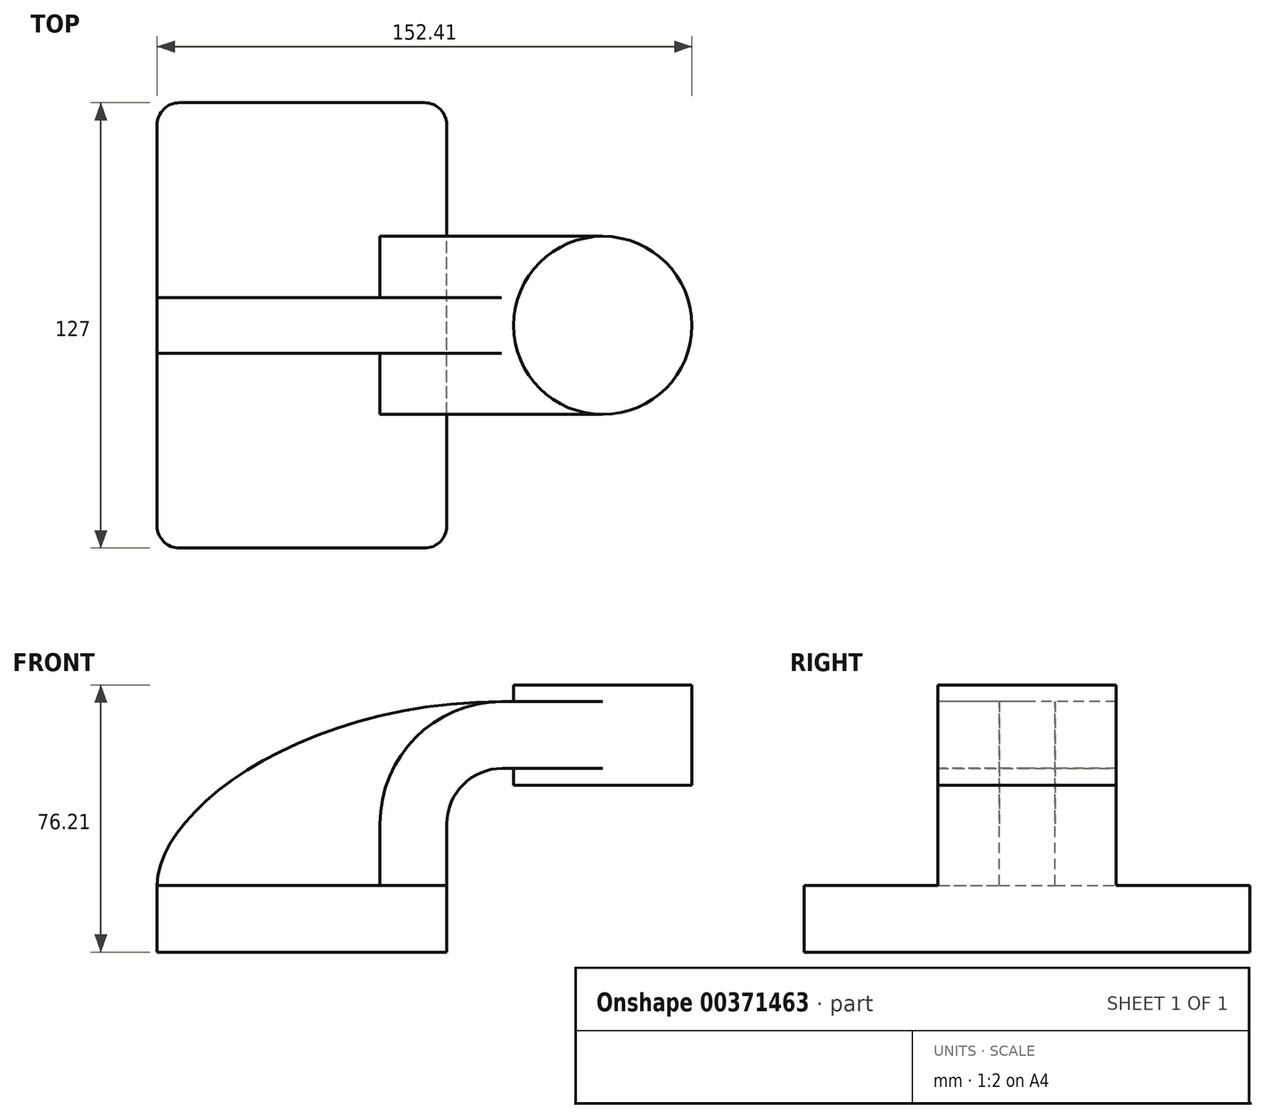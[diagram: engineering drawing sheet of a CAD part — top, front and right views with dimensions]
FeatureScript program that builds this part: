
annotation { "Feature Type Name" : "Feature", "Feature Type Description" : "" }
export const myFeature = defineFeature(function(context is Context, id is Id, definition is map)
    precondition{}
    {
        {
            var Q0;
            Q0=qCreatedBy(makeId("Front.planeOp"),FACE);
            var sketch = newSketch(context, id + "F0", { "sketchPlane" : qUnion([Q0])});
            skLineSegment(sketch, "E0.bottom", {"start": v(-41.27, -9.53) * mm, "end": v(41.28, -9.53) * mm});
            skLineSegment(sketch, "E0.top", {"start": v(-41.28, 9.52) * mm, "end": v(41.28, 9.52) * mm});
            skLineSegment(sketch, "E0.left", {"start": v(-41.28, -9.53) * mm, "end": v(-41.28, 9.52) * mm});
            skLineSegment(sketch, "E0.right", {"start": v(41.28, -9.53) * mm, "end": v(41.28, 9.52) * mm});
            skPoint(sketch, "E0.middle", {"position": v(0, 0) * mm});
            skLineSegment(sketch, "E1.bottom", {"start": v(60.33, 38.1) * mm, "end": v(111.12, 38.1) * mm});
            skLineSegment(sketch, "E1.top", {"start": v(60.33, 66.67) * mm, "end": v(111.12, 66.67) * mm});
            skLineSegment(sketch, "E1.left", {"start": v(60.33, 38.1) * mm, "end": v(60.33, 66.67) * mm});
            skLineSegment(sketch, "E1.right", {"start": v(111.12, 38.1) * mm, "end": v(111.12, 66.67) * mm});
            skPoint(sketch, "E1.middle", {"position": v(85.72, 52.39) * mm});
            skLineSegment(sketch, "E2", {"start": v(41.27, 9.52) * mm, "end": v(41.27, 27) * mm});
            skArc(sketch, "E3", {"start": v(57.15, 42.88) * mm, "mid": v(45.92, 38.23) * mm, "end": v(41.27, 27) * mm});
            skLineSegment(sketch, "E4", {"start": v(57.15, 42.88) * mm, "end": v(85.72, 42.88) * mm});
            skLineSegment(sketch, "E5.0", {"start": v(22.23, 9.52) * mm, "end": v(22.23, 27) * mm});
            skArc(sketch, "E5.1", {"start": v(57.15, 61.93) * mm, "mid": v(32.45, 51.7) * mm, "end": v(22.22, 27) * mm});
            skLineSegment(sketch, "E5.2", {"start": v(57.15, 61.93) * mm, "end": v(85.72, 61.93) * mm});
            skLineSegment(sketch, "E6", {"start": v(85.72, 38.1) * mm, "end": v(85.72, 66.67) * mm});
            skFitSpline(sketch, "E7", {"points": [v(-41.28, 9.52) * mm, v(57.15, 61.93) * mm], "startDerivative": vector(0.89, 64.7) * mm, "endDerivative": vector(171.45, 0.51) * mm});
            skSolve(sketch);
        }
        {
            var Q0;
            Q0=makeQuery(id+"F0.imprint","IMPRINT",FACE,{"disambiguationData":[TD([[makeQuery(id+"F0.imprint","IMPRINT",EDGE,{"derivedFrom":sQuery(id+"F0.wireOp",EDGE,"E0.bottom")}),1.0]])]});
            extrude(context, id + "F1", {"entities" : qUnion([Q0]), "endBound" : BoundingType.SYMMETRIC, "depth" : 127 * mm});
        }
        {
            var Q0;
            {var subQ5=sQuery(id+"F0.wireOp",EDGE,"E2");Q0=makeQuery(id+"F0.imprint","IMPRINT",FACE,{"disambiguationData":[TD([[makeQuery(id+"F0.imprint","IMPRINT",EDGE,{"derivedFrom":subQ5}),1.0]])]});}
            var Q1;
            {var subQ0=sQuery(id+"F0.wireOp",EDGE,"E4");var subQ1=sQuery(id+"F0.wireOp",EDGE,"E1.left");var subQ2=makeQuery(id+"F0.imprint","INTERSECT",VERTEX,{"derivedFrom":[subQ1,subQ0]});Q1=makeQuery(id+"F0.imprint","IMPRINT",FACE,{"disambiguationData":[TD([[makeQuery(id+"F0.imprint","IMPRINT",EDGE,{"disambiguationData":[TD([[subQ2,-1.0]])],"derivedFrom":subQ1}),-1.0]])]});}
            extrude(context, id + "F2", {"entities" : qUnion([Q0, Q1]), "operationType" : NewBodyOperationType.ADD, "endBound" : BoundingType.SYMMETRIC, "depth" : 50.8 * mm});
        }
        {
            var Q0;
            {var subQ3=sQuery(id+"F0.wireOp",EDGE,"E5.0");Q0=makeQuery(id+"F0.imprint","IMPRINT",FACE,{"disambiguationData":[TD([[makeQuery(id+"F0.imprint","IMPRINT",EDGE,{"derivedFrom":subQ3}),1.0]])]});}
            extrude(context, id + "F3", {"entities" : qUnion([Q0]), "operationType" : NewBodyOperationType.ADD, "endBound" : BoundingType.SYMMETRIC, "depth" : 15.88 * mm});
        }
        {
            var Q0;
            {var subQ0=sQuery(id+"F0.wireOp",EDGE,"E1.right");Q0=makeQuery(id+"F0.imprint","IMPRINT",FACE,{"disambiguationData":[TD([[makeQuery(id+"F0.imprint","IMPRINT",EDGE,{"derivedFrom":subQ0}),1.0]])]});}
            var Q1;
            Q1=sQuery(id+"F0.wireOp",EDGE,"E6");
            revolve(context, id + "F4", {"operationType" : NewBodyOperationType.ADD, "entities" : qUnion([Q0]), "axis" : qUnion([Q1]), "revolveType" : RevolveType.FULL});
        }
        {
            var Q0;
            Q0=makeQuery(id+"F1.opExtrude","CAP_EDGE",EDGE,{"disambiguationData":[OSD([sQuery(id+"F0.wireOp",EDGE,"E0.right")])],"isStart":false});
            var Q1;
            Q1=makeQuery(id+"F1.opExtrude","CAP_EDGE",EDGE,{"disambiguationData":[OSD([sQuery(id+"F0.wireOp",EDGE,"E0.right")])],"isStart":true});
            var Q2;
            Q2=makeQuery(id+"F1.opExtrude","CAP_EDGE",EDGE,{"disambiguationData":[OSD([sQuery(id+"F0.wireOp",EDGE,"E0.left")])],"isStart":false});
            var Q3;
            Q3=makeQuery(id+"F1.opExtrude","CAP_EDGE",EDGE,{"disambiguationData":[OSD([sQuery(id+"F0.wireOp",EDGE,"E0.left")])],"isStart":true});
            fillet(context, id + "F5", {"entities" : qUnion([Q0, Q1, Q2, Q3]), "radius" : 6.35 * mm, "tangentPropagation" : true, "allowEdgeOverflow" : false});
        }
    });
